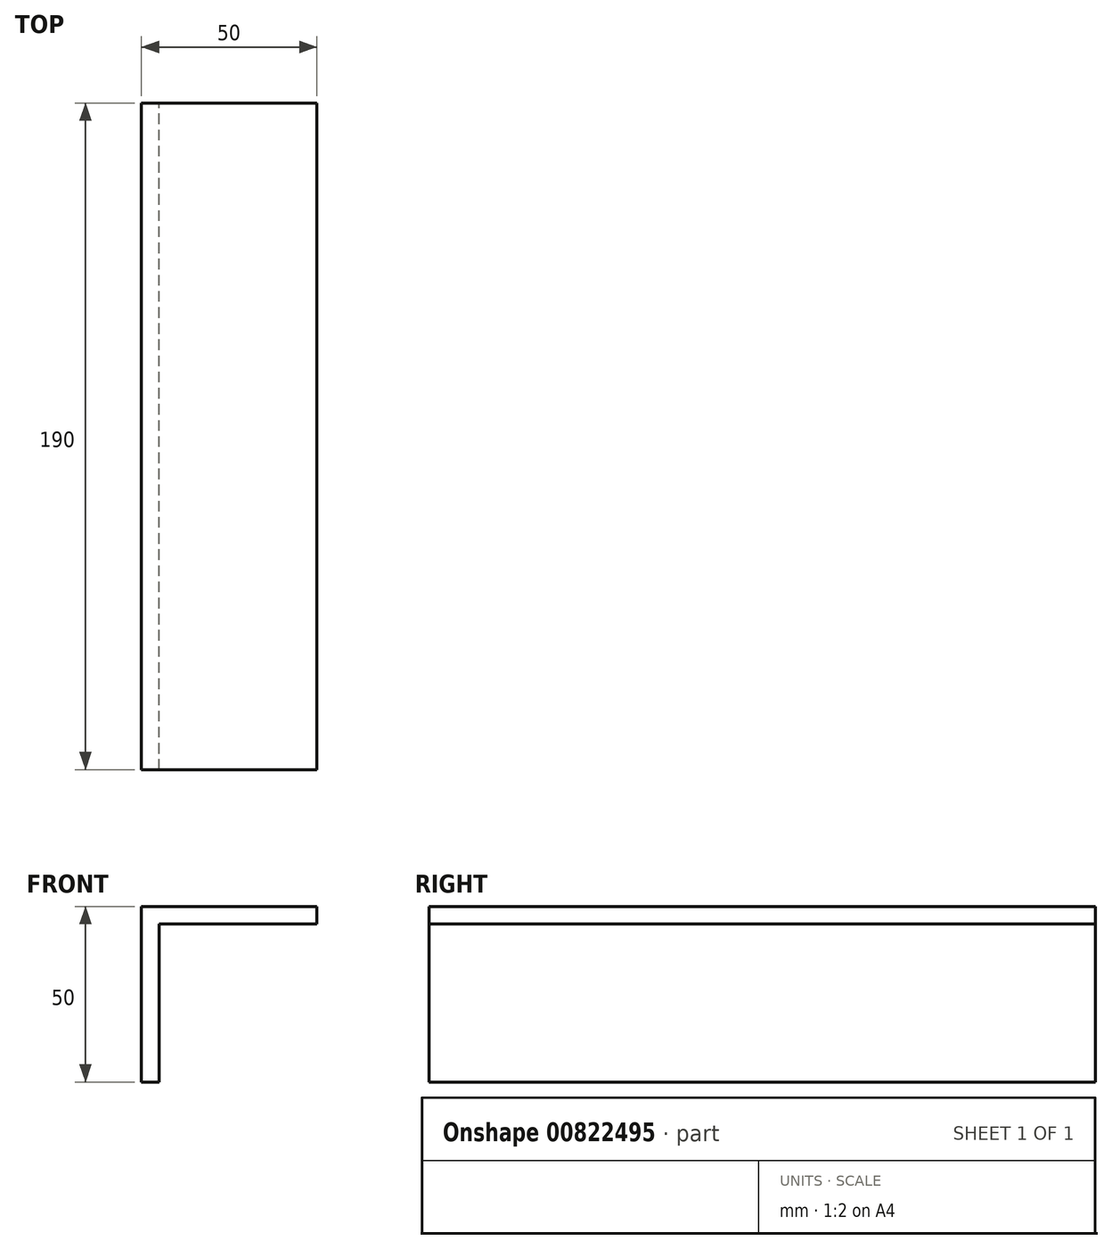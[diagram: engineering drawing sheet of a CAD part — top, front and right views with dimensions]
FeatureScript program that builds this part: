
annotation { "Feature Type Name" : "Feature", "Feature Type Description" : "" }
export const myFeature = defineFeature(function(context is Context, id is Id, definition is map)
    precondition{}
    {
        {
            var Q0;
            Q0=qCreatedBy(makeId("Front.planeOp"),FACE);
            var sketch = newSketch(context, id + "F0", { "sketchPlane" : qUnion([Q0])});
            skLineSegment(sketch, "E0", {"start": v(0, 0) * mm, "end": v(0, 50) * mm});
            skLineSegment(sketch, "E1", {"start": v(0, 50) * mm, "end": v(50, 50) * mm});
            skLineSegment(sketch, "E2", {"start": v(50, 50) * mm, "end": v(50, 45) * mm});
            skLineSegment(sketch, "E3", {"start": v(50, 45) * mm, "end": v(5, 45) * mm});
            skLineSegment(sketch, "E4", {"start": v(5, 45) * mm, "end": v(5, 0) * mm});
            skLineSegment(sketch, "E5", {"start": v(5, 0) * mm, "end": v(0, 0) * mm});
            skSolve(sketch);
        }
        {
            var Q0;
            Q0=makeQuery(id+"F0.imprint","IMPRINT",FACE,{"disambiguationData":[TD([[makeQuery(id+"F0.imprint","IMPRINT",EDGE,{"derivedFrom":sQuery(id+"F0.wireOp",EDGE,"E0")}),-1.0]])]});
            extrude(context, id + "F1", {"entities" : qUnion([Q0]), "depth" : 190 * mm, "offsetDistance" : 25 * mm});
        }
    });
